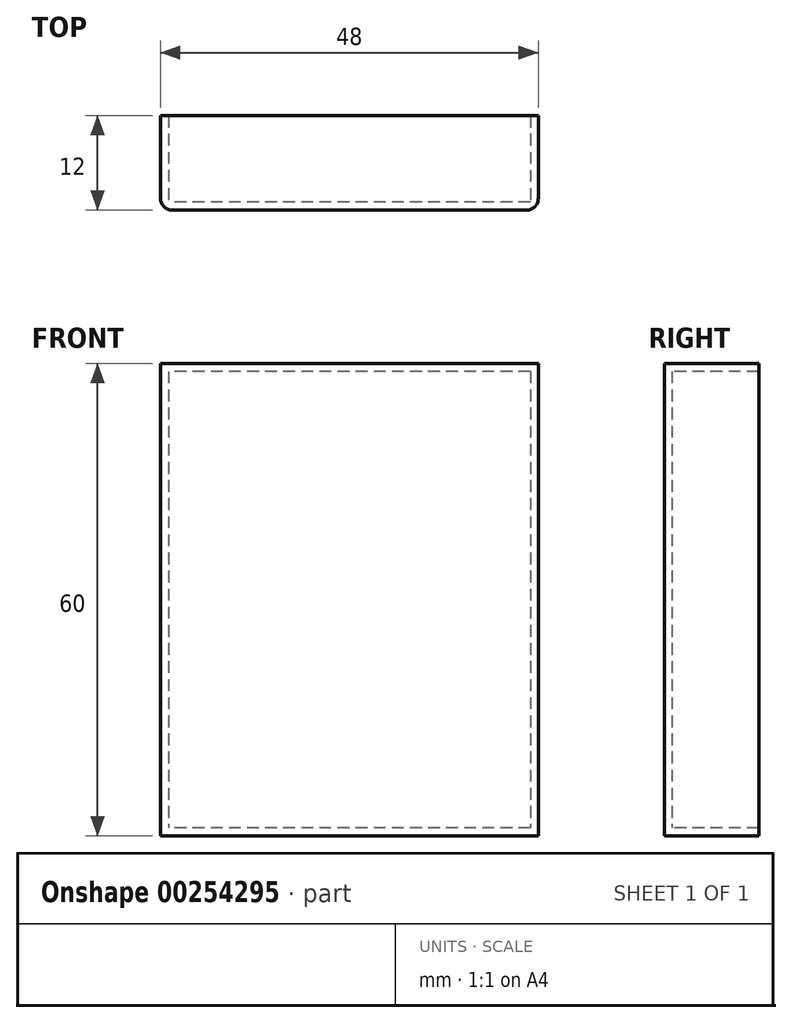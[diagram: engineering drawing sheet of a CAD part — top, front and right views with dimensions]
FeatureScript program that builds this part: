
annotation { "Feature Type Name" : "Feature", "Feature Type Description" : "" }
export const myFeature = defineFeature(function(context is Context, id is Id, definition is map)
    precondition{}
    {
        {
            var Q0;
            Q0=qCreatedBy(makeId("Top.planeOp"),FACE);
            var sketch = newSketch(context, id + "F0", { "sketchPlane" : qUnion([Q0])});
            skLineSegment(sketch, "E0.bottom", {"start": v(24, 6) * mm, "end": v(-24, 6) * mm});
            skLineSegment(sketch, "E0.top", {"start": v(24, -6) * mm, "end": v(-24, -6) * mm});
            skLineSegment(sketch, "E0.left", {"start": v(24, 6) * mm, "end": v(24, -6) * mm});
            skLineSegment(sketch, "E0.right", {"start": v(-24, 6) * mm, "end": v(-24, -6) * mm});
            skPoint(sketch, "E0.middle", {"position": v(0, 0) * mm});
            skSolve(sketch);
        }
        {
            var Q0;
            Q0=makeQuery(id+"F0.imprint","IMPRINT",FACE,{"disambiguationData":[TD([[makeQuery(id+"F0.imprint","IMPRINT",EDGE,{"derivedFrom":sQuery(id+"F0.wireOp",EDGE,"E0.bottom")}),1.0]])]});
            extrude(context, id + "F1", {"entities" : qUnion([Q0]), "depth" : 60 * mm});
        }
        {
            var Q0;
            Q0=makeQuery(id+"F1.opExtrude","SWEPT_FACE",FACE,{"disambiguationData":[OSD([sQuery(id+"F0.wireOp",EDGE,"E0.bottom")])]});
            shell(context, id + "F2", {"entities" : qUnion([Q0]), "thickness" : 1 * mm});
        }
        {
            var Q0;
            Q0=makeQuery(id+"F1.opExtrude","SWEPT_EDGE",EDGE,{"disambiguationData":[OSD([sQuery(id+"F0.wireOp",EDGE,"E0.top"),sQuery(id+"F0.wireOp",EDGE,"E0.left")])]});
            var Q1;
            Q1=makeQuery(id+"F1.opExtrude","SWEPT_EDGE",EDGE,{"disambiguationData":[OSD([sQuery(id+"F0.wireOp",EDGE,"E0.top"),sQuery(id+"F0.wireOp",EDGE,"E0.right")])]});
            fillet(context, id + "F3", {"entities" : qUnion([Q0, Q1]), "radius" : 1.5 * mm, "tangentPropagation" : true, "allowEdgeOverflow" : false});
        }
    });
